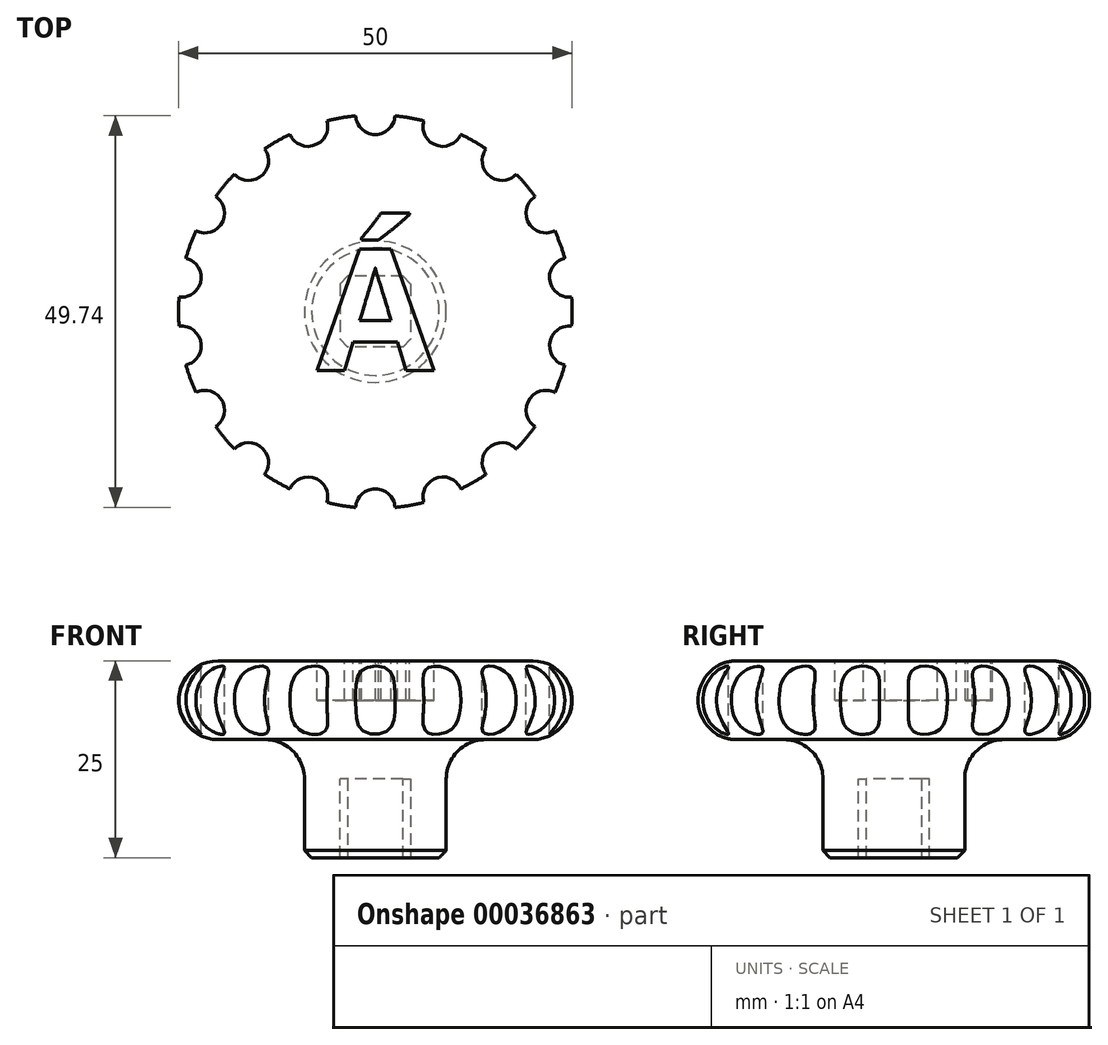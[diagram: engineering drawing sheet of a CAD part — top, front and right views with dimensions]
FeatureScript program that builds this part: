
annotation { "Feature Type Name" : "Feature", "Feature Type Description" : "" }
export const myFeature = defineFeature(function(context is Context, id is Id, definition is map)
    precondition{}
    {
        {
            var Q0;
            Q0=qCreatedBy(makeId("Top.planeOp"),FACE);
            var sketch = newSketch(context, id + "F0", { "sketchPlane" : qUnion([Q0])});
            skLineSegment(sketch, "E0.rect.bottom", {"start": v(4.5, 4.5) * mm, "end": v(-4.5, 4.5) * mm});
            skLineSegment(sketch, "E0.rect.top", {"start": v(4.5, -4.5) * mm, "end": v(-4.5, -4.5) * mm});
            skLineSegment(sketch, "E0.rect.left", {"start": v(4.5, 4.5) * mm, "end": v(4.5, -4.5) * mm});
            skLineSegment(sketch, "E0.rect.right", {"start": v(-4.5, 4.5) * mm, "end": v(-4.5, -4.5) * mm});
            skPoint(sketch, "E0.rect.middle", {"position": v(0, 0) * mm});
            skCircle(sketch, "E1", {"center": v(0, 0) * mm, "radius": 9 * mm});
            skSolve(sketch);
        }
        {
            var Q0;
            Q0=makeQuery(id+"F0.imprint","IMPRINT",FACE,{"disambiguationData":[TD([[makeQuery(id+"F0.imprint","IMPRINT",EDGE,{"derivedFrom":sQuery(id+"F0.wireOp",EDGE,"E0.rect.bottom")}),-1.0]])]});
            var Q1;
            Q1=makeQuery(id+"F0.imprint","IMPRINT",FACE,{"disambiguationData":[TD([[makeQuery(id+"F0.imprint","IMPRINT",EDGE,{"derivedFrom":sQuery(id+"F0.wireOp",EDGE,"E0.rect.bottom")}),1.0]])]});
            extrude(context, id + "F1", {"entities" : qUnion([Q0, Q1]), "depth" : 15 * mm});
        }
        {
            var Q0;
            Q0=makeQuery(id+"F0.imprint","IMPRINT",FACE,{"disambiguationData":[TD([[makeQuery(id+"F0.imprint","IMPRINT",EDGE,{"derivedFrom":sQuery(id+"F0.wireOp",EDGE,"E0.rect.bottom")}),1.0]])]});
            extrude(context, id + "F2", {"entities" : qUnion([Q0]), "operationType" : NewBodyOperationType.REMOVE, "depth" : 10 * mm});
        }
        {
            var Q0;
            Q0=makeQuery(id+"F2.boolean.opBoolean","COPY",EDGE,{"derivedFrom":makeQuery(id+"F2.opExtrude","SWEPT_EDGE",EDGE,{"disambiguationData":[OSD([sQuery(id+"F0.wireOp",EDGE,"E0.rect.top"),sQuery(id+"F0.wireOp",EDGE,"E0.rect.right")])]})});
            var Q1;
            Q1=makeQuery(id+"F2.boolean.opBoolean","COPY",EDGE,{"derivedFrom":makeQuery(id+"F2.opExtrude","SWEPT_EDGE",EDGE,{"disambiguationData":[OSD([sQuery(id+"F0.wireOp",EDGE,"E0.rect.bottom"),sQuery(id+"F0.wireOp",EDGE,"E0.rect.right")])]})});
            var Q2;
            Q2=makeQuery(id+"F2.boolean.opBoolean","COPY",EDGE,{"derivedFrom":makeQuery(id+"F2.opExtrude","SWEPT_EDGE",EDGE,{"disambiguationData":[OSD([sQuery(id+"F0.wireOp",EDGE,"E0.rect.bottom"),sQuery(id+"F0.wireOp",EDGE,"E0.rect.left")])]})});
            var Q3;
            Q3=makeQuery(id+"F2.boolean.opBoolean","COPY",EDGE,{"derivedFrom":makeQuery(id+"F2.opExtrude","SWEPT_EDGE",EDGE,{"disambiguationData":[OSD([sQuery(id+"F0.wireOp",EDGE,"E0.rect.top"),sQuery(id+"F0.wireOp",EDGE,"E0.rect.left")])]})});
            var Q4;
            Q4=makeQuery(id+"F2.boolean.opBoolean","COPY",EDGE,{"derivedFrom":makeQuery(id+"F2.opExtrude","CAP_EDGE",EDGE,{"disambiguationData":[OSD([sQuery(id+"F0.wireOp",EDGE,"E0.rect.top")])],"isStart":true})});
            chamfer(context, id + "F3", {"entities" : qUnion([Q0, Q1, Q2, Q3, Q4]), "width" : 1 * mm, "tangentPropagation" : true});
        }
        {
            var Q0;
            Q0=makeQuery(id+"F1.opExtrude","CAP_FACE",FACE,{"disambiguationData":[OSD([sQuery(id+"F0.wireOp",EDGE,"E1")])],"isStart":false});
            var sketch = newSketch(context, id + "F4", { "sketchPlane" : qUnion([Q0])});
            skCircle(sketch, "E2", {"center": v(0, 0) * mm, "radius": 25 * mm});
            skSolve(sketch);
        }
        {
            var Q0;
            Q0=qSketchRegion(id+"F4",true);
            var Q1;
            Q1=makeQuery(id+"F4.imprint","IMPRINT",FACE,{"disambiguationData":[TD([[makeQuery(id+"F4.imprint","IMPRINT",EDGE,{"derivedFrom":sQuery(id+"F4.wireOp",EDGE,"E2")}),1.0]])]});
            extrude(context, id + "F5", {"entities" : qUnion([Q0, Q1]), "operationType" : NewBodyOperationType.ADD, "depth" : 10 * mm});
        }
        {
            var Q0;
            Q0=makeQuery(id+"F1.opExtrude","CAP_EDGE",EDGE,{"disambiguationData":[OSD([sQuery(id+"F0.wireOp",EDGE,"E1")])],"isStart":false});
            var Q1;
            Q1=makeQuery(id+"F5.opExtrude","CAP_EDGE",EDGE,{"disambiguationData":[OSD([sQuery(id+"F4.wireOp",EDGE,"E2")])],"isStart":false});
            var Q2;
            Q2=makeQuery(id+"F5.opExtrude","CAP_FACE",FACE,{"disambiguationData":[OSD([sQuery(id+"F4.wireOp",EDGE,"E2")])],"isStart":true});
            fillet(context, id + "F6", {"entities" : qUnion([Q0, Q1, Q2]), "radius" : 5 * mm, "tangentPropagation" : true, "allowEdgeOverflow" : false});
        }
        {
            var Q0;
            Q0=makeQuery(id+"F5.opExtrude","CAP_FACE",FACE,{"disambiguationData":[OSD([sQuery(id+"F4.wireOp",EDGE,"E2")])],"isStart":false});
            var sketch = newSketch(context, id + "F7", { "sketchPlane" : qUnion([Q0])});
            skText(sketch, "E3", { "text": "Á", "fontName": "OpenSans-Bold.ttf"});
            const initialGuessF7  = {"E3": [-0.00743, -0.0075, 1, 0, 0.0155]};
            skSetInitialGuess(sketch, initialGuessF7);
            skSolve(sketch);
        }
        {
            var Q0;
            Q0=makeQuery(id+"F7.imprint","IMPRINT",FACE,{"disambiguationData":[TD([[makeQuery(id+"F7.imprint","IMPRINT",EDGE,{"derivedFrom":sQuery(id+"F7.wireOp",EDGE,"E3.sketch_text.stroke-0")}),-1.0]])]});
            var Q1;
            Q1=qSketchRegion(id+"F7",true);
            extrude(context, id + "F8", {"entities" : qUnion([Q0, Q1]), "operationType" : NewBodyOperationType.REMOVE, "oppositeDirection" : true, "depth" : 5 * mm});
        }
        {
            var Q0;
            Q0=makeQuery(id+"F5.opExtrude","CAP_FACE",FACE,{"disambiguationData":[OSD([sQuery(id+"F4.wireOp",EDGE,"E2")])],"isStart":false});
            var sketch = newSketch(context, id + "F9", { "sketchPlane" : qUnion([Q0])});
            skCircle(sketch, "E4", {"center": v(0, -25) * mm, "radius": 2.5 * mm});
            skCircle(sketch, "E5.1.0", {"center": v(8.55, -23.5) * mm, "radius": 2.5 * mm});
            skCircle(sketch, "E5.2.0", {"center": v(16.07, -19.15) * mm, "radius": 2.5 * mm});
            skCircle(sketch, "E5.3.0", {"center": v(21.65, -12.5) * mm, "radius": 2.5 * mm});
            skCircle(sketch, "E5.4.0", {"center": v(24.62, -4.34) * mm, "radius": 2.5 * mm});
            skCircle(sketch, "E5.5.0", {"center": v(24.62, 4.34) * mm, "radius": 2.5 * mm});
            skCircle(sketch, "E5.6.0", {"center": v(21.65, 12.5) * mm, "radius": 2.5 * mm});
            skCircle(sketch, "E5.7.0", {"center": v(16.07, 19.15) * mm, "radius": 2.5 * mm});
            skCircle(sketch, "E5.8.0", {"center": v(8.55, 23.5) * mm, "radius": 2.5 * mm});
            skCircle(sketch, "E5.9.0", {"center": v(0, 25) * mm, "radius": 2.5 * mm});
            skCircle(sketch, "E5.10.0", {"center": v(-8.55, 23.5) * mm, "radius": 2.5 * mm});
            skCircle(sketch, "E5.11.0", {"center": v(-16.07, 19.15) * mm, "radius": 2.5 * mm});
            skCircle(sketch, "E5.12.0", {"center": v(-21.65, 12.5) * mm, "radius": 2.5 * mm});
            skCircle(sketch, "E5.13.0", {"center": v(-24.62, 4.34) * mm, "radius": 2.5 * mm});
            skCircle(sketch, "E5.14.0", {"center": v(-24.62, -4.34) * mm, "radius": 2.5 * mm});
            skPoint(sketch, "E5.center", {"position": v(0, 0) * mm});
            skCircle(sketch, "E6.1.15.0", {"center": v(-21.65, -12.5) * mm, "radius": 2.5 * mm});
            skCircle(sketch, "E6.1.16.0", {"center": v(-16.07, -19.15) * mm, "radius": 2.5 * mm});
            skCircle(sketch, "E6.1.17.0", {"center": v(-8.55, -23.5) * mm, "radius": 2.5 * mm});
            skCircle(sketch, "E7", {"center": v(0, 0) * mm, "radius": 25 * mm, "construction": true});
            skSolve(sketch);
        }
        {
            var Q0;
            Q0=qSketchRegion(id+"F9",true);
            extrude(context, id + "F10", {"entities" : qUnion([Q0]), "operationType" : NewBodyOperationType.REMOVE, "oppositeDirection" : true, "depth" : 25 * mm});
        }
        {
            var Q0;
            Q0=makeQuery(id+"F1.opExtrude","CAP_EDGE",EDGE,{"disambiguationData":[OSD([sQuery(id+"F0.wireOp",EDGE,"E1")])],"isStart":true});
            chamfer(context, id + "F11", {"entities" : qUnion([Q0]), "width" : .9 * mm, "tangentPropagation" : true});
        }
    });
